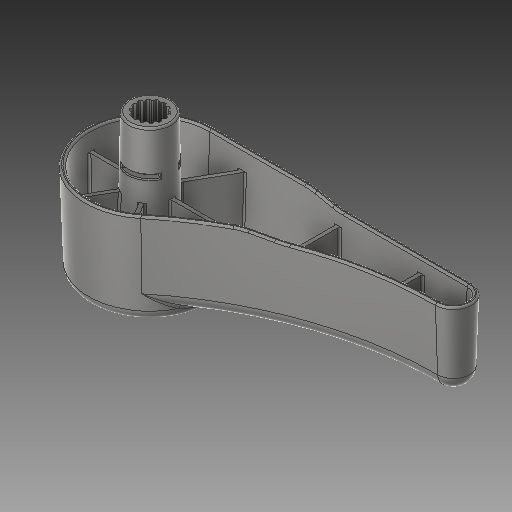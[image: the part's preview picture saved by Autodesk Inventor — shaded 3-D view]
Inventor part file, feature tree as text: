
AUTODESK INVENTOR PART (.ipt)
format: ipt  version: 2019 (Build 230136000, 136)  size: 1,799,168 bytes
history: native  units: in
note: dims shown in document units (in); Inventor stores cm internally (conversion verified against a paired STEP export)
features: sketch x10, plane x4, other x3
ambient origin geometry x8: Origin, YZ Plane, XZ Plane, XY Plane, X Axis, Y Axis, Z Axis, Center Point
bodies: Solid1 (feature_tree)
feature tree (17):
  other  "Handle.ipt"
  other  "Solid1::Handle.ipt"
  other  "TaggingFeature1"
  sketch  "Sketch8"  dims[d0=0.3937in]
  sketch  "Sketch9"
  sketch  "Sketch10"
  sketch  "Sketch11"
  sketch  "Sketch12"
  sketch  "Sketch13"
  sketch  "Sketch19"
  sketch  "Sketch21"
  sketch  "Sketch22"
  sketch  "Sketch23"
  plane  "Work Plane1"
  plane  "Work Plane2"
  plane  "Work Plane3"
  plane  "Work Plane10"
